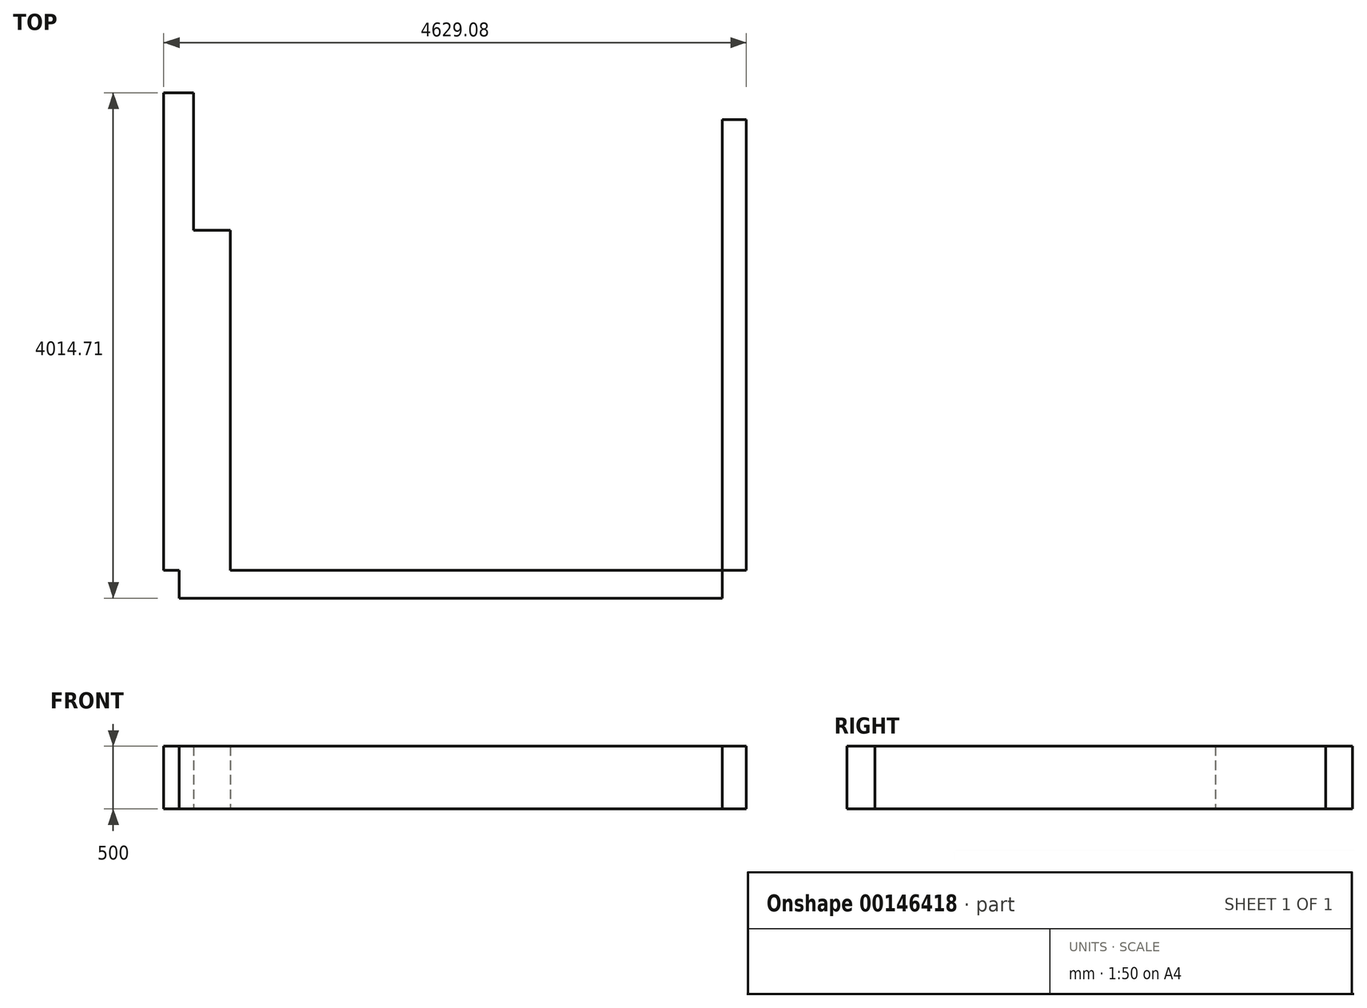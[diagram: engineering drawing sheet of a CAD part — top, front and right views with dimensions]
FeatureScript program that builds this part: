
annotation { "Feature Type Name" : "Feature", "Feature Type Description" : "" }
export const myFeature = defineFeature(function(context is Context, id is Id, definition is map)
    precondition{}
    {
        {
            var Q0;
            Q0=qCreatedBy(makeId("Top.planeOp"),FACE);
            var sketch = newSketch(context, id + "F0", { "sketchPlane" : qUnion([Q0])});
            skLineSegment(sketch, "E0.bottom", {"start": v(-4152.46, 3536.7) * mm, "end": v(47.54, 3536.7) * mm});
            skLineSegment(sketch, "E0.top", {"start": v(-4152.46, -43.3) * mm, "end": v(47.54, -43.3) * mm});
            skLineSegment(sketch, "E0.left", {"start": v(-4152.46, 3536.7) * mm, "end": v(-4152.46, -43.3) * mm});
            skLineSegment(sketch, "E0.right", {"start": v(47.54, 3536.7) * mm, "end": v(47.54, -43.3) * mm});
            skLineSegment(sketch, "E1.bottom", {"start": v(-4152.46, -43.3) * mm, "end": v(-3862.74, -43.3) * mm});
            skLineSegment(sketch, "E1.top", {"start": v(-4152.46, 2659.39) * mm, "end": v(-3862.74, 2659.39) * mm});
            skLineSegment(sketch, "E1.left", {"start": v(-4152.46, -43.3) * mm, "end": v(-4152.46, 2659.39) * mm});
            skLineSegment(sketch, "E1.right", {"start": v(-3862.74, -43.3) * mm, "end": v(-3862.74, 2659.39) * mm});
            skLineSegment(sketch, "E2", {"start": v(-3547.76, 3536.7) * mm, "end": v(-3547.76, 2736.7) * mm});
            skArc(sketch, "E3", {"start": v(-3547.76, 2736.7) * mm, "mid": v(-2982.08, 2971.02) * mm, "end": v(-2747.76, 3536.7) * mm});
            skLineSegment(sketch, "E4.left", {"start": v(-4152.46, 3536.7) * mm, "end": v(-4152.46, 3763.53) * mm});
            skLineSegment(sketch, "E4.right", {"start": v(47.54, 3536.7) * mm, "end": v(47.54, 3763.53) * mm});
            skLineSegment(sketch, "E5.bottom", {"start": v(47.54, 3536.7) * mm, "end": v(238.92, 3536.7) * mm});
            skLineSegment(sketch, "E5.top", {"start": v(47.54, -43.3) * mm, "end": v(238.92, -43.3) * mm});
            skLineSegment(sketch, "E5.right", {"start": v(238.92, 3536.7) * mm, "end": v(238.92, -43.3) * mm});
            skLineSegment(sketch, "E6.bottom", {"start": v(47.54, -43.3) * mm, "end": v(-4268.57, -43.3) * mm});
            skLineSegment(sketch, "E6.top", {"start": v(47.54, -265.2) * mm, "end": v(-4268.57, -265.2) * mm});
            skLineSegment(sketch, "E6.left", {"start": v(47.54, -43.3) * mm, "end": v(47.54, -265.2) * mm});
            skLineSegment(sketch, "E6.right", {"start": v(-4268.57, -43.3) * mm, "end": v(-4268.57, -265.2) * mm});
            skLineSegment(sketch, "E7.bottom", {"start": v(-4152.46, -43.3) * mm, "end": v(-4390.16, -43.3) * mm});
            skLineSegment(sketch, "E7.top", {"start": v(-4152.46, 3749.51) * mm, "end": v(-4390.16, 3749.51) * mm});
            skLineSegment(sketch, "E7.left", {"start": v(-4152.46, -43.3) * mm, "end": v(-4152.46, 3749.51) * mm});
            skLineSegment(sketch, "E7.right", {"start": v(-4390.16, -43.3) * mm, "end": v(-4390.16, 3749.51) * mm});
            skLineSegment(sketch, "E8.bottom", {"start": v(-3547.76, 3536.7) * mm, "end": v(-4152.46, 3536.7) * mm});
            skLineSegment(sketch, "E8.top", {"start": v(-3547.76, 3763.53) * mm, "end": v(-4152.46, 3763.53) * mm});
            skLineSegment(sketch, "E8.left", {"start": v(-3547.76, 3536.7) * mm, "end": v(-3547.76, 3763.53) * mm});
            skLineSegment(sketch, "E9.bottom", {"start": v(-2747.76, 3536.7) * mm, "end": v(47.54, 3536.7) * mm});
            skLineSegment(sketch, "E9.top", {"start": v(-2747.76, 3763.53) * mm, "end": v(47.54, 3763.53) * mm});
            skLineSegment(sketch, "E9.left", {"start": v(-2747.76, 3536.7) * mm, "end": v(-2747.76, 3763.53) * mm});
            skLineSegment(sketch, "E10.bottom", {"start": v(-3547.76, 3536.7) * mm, "end": v(-3640.58, 3536.7) * mm});
            skLineSegment(sketch, "E10.top", {"start": v(-3547.76, 2718.34) * mm, "end": v(-3640.58, 2718.34) * mm});
            skLineSegment(sketch, "E10.left", {"start": v(-3547.76, 3536.7) * mm, "end": v(-3547.76, 2718.34) * mm});
            skLineSegment(sketch, "E10.right", {"start": v(-3640.58, 3536.7) * mm, "end": v(-3640.58, 2718.34) * mm});
            skSolve(sketch);
        }
        {
            var Q0;
            Q0=makeQuery(id+"F0.imprint","IMPRINT",FACE,{"disambiguationData":[TD([[makeQuery(id+"F0.imprint","IMPRINT",EDGE,{"derivedFrom":sQuery(id+"F0.wireOp",EDGE,"E5.bottom")}),-1.0]])]});
            var Q1;
            Q1=makeQuery(id+"F0.imprint","IMPRINT",FACE,{"disambiguationData":[TD([[makeQuery(id+"F0.imprint","IMPRINT",EDGE,{"derivedFrom":sQuery(id+"F0.wireOp",EDGE,"E9.bottom")}),1.0]])]});
            var Q2;
            {var subQ2=sQuery(id+"F0.wireOp",EDGE,"E8.bottom");Q2=makeQuery(id+"F0.imprint","IMPRINT",FACE,{"disambiguationData":[TD([[makeQuery(id+"F0.imprint","IMPRINT",EDGE,{"derivedFrom":subQ2}),-1.0]])]});}
            var Q3;
            Q3=makeQuery(id+"F0.imprint","IMPRINT",FACE,{"disambiguationData":[TD([[makeQuery(id+"F0.imprint","IMPRINT",EDGE,{"derivedFrom":sQuery(id+"F0.wireOp",EDGE,"E6.top")}),-1.0]])]});
            var Q4;
            {var subQ4=sQuery(id+"F0.wireOp",EDGE,"E7.top");Q4=makeQuery(id+"F0.imprint","IMPRINT",FACE,{"disambiguationData":[TD([[makeQuery(id+"F0.imprint","IMPRINT",EDGE,{"derivedFrom":subQ4}),1.0]])]});}
            var Q5;
            {var subQ0=sQuery(id+"F0.wireOp",EDGE,"E1.top");Q5=makeQuery(id+"F0.imprint","IMPRINT",FACE,{"disambiguationData":[TD([[makeQuery(id+"F0.imprint","IMPRINT",EDGE,{"derivedFrom":subQ0}),-1.0]])]});}
            extrude(context, id + "F1", {"entities" : qUnion([Q0, Q1, Q2, Q3, Q4, Q5]), "depth" : 500 * mm});
        }
    });
